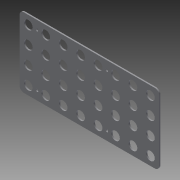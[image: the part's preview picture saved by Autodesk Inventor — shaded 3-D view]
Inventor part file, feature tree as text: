
AUTODESK INVENTOR PART (.ipt)
format: ipt  version: 2015 SP1 (Build 190203100, 203)  size: 445,440 bytes
history: native  units: in
note: dims shown in document units (in); Inventor stores cm internally (conversion verified against a paired STEP export)
features: extrude x2, sketch x2, fillet x1
ambient origin geometry x8: Origin, YZ Plane, XZ Plane, XY Plane, X Axis, Y Axis, Z Axis, Center Point
bodies: Solid1 (feature_tree)
feature tree (5):
  extrude  "Extrusion1"  Depth=0.7874in
  extrude  "Extrusion2"  Depth=0.1969in
  fillet  "Fillet1"  Radius=0.0591in
  sketch  "Sketch1"  dims[d0=0.7874in d1=0.7874in]
  sketch  "Sketch2"  dims[d2=0.7874in d3=0.7874in d4=0.0591in d5=0.0in d6=0.3937in d7=0.3937in d8=0.3937in d9=3.1496in d11=0.7874in d12=1.5748in d14=0.7874in d17=0.7874in d18=0.0in d19=6.2992in d20=3.1496in d21=0.1969in]
